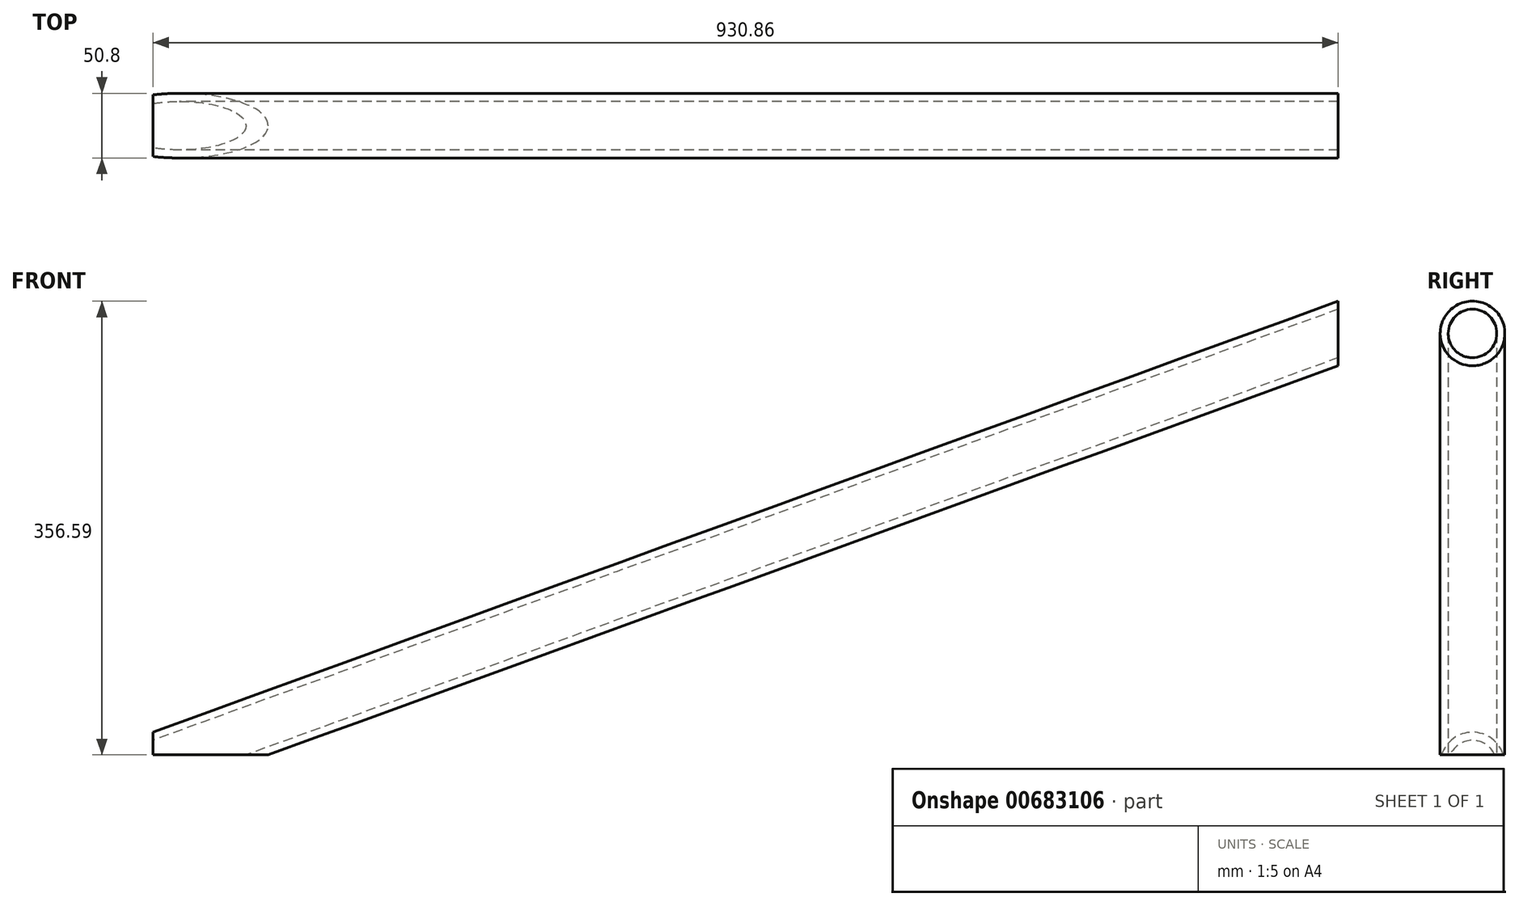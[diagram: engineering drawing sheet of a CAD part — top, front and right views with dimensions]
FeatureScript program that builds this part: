
annotation { "Feature Type Name" : "Feature", "Feature Type Description" : "" }
export const myFeature = defineFeature(function(context is Context, id is Id, definition is map)
    precondition{}
    {
        {
            var Q0;
            Q0=qCreatedBy(makeId("Front.planeOp"),FACE);
            var sketch = newSketch(context, id + "F0", { "sketchPlane" : qUnion([Q0])});
            skLineSegment(sketch, "E0", {"start": v(0, 0) * mm, "end": v(930.86, 338.8) * mm});
            skSolve(sketch);
        }
        {
            var Q0;
            Q0=qCreatedBy(makeId("Right.planeOp"),FACE);
            var sketch = newSketch(context, id + "F1", { "sketchPlane" : qUnion([Q0])});
            skCircle(sketch, "E1", {"center": v(0, 0) * mm, "radius": 25.4 * mm});
            skCircle(sketch, "E2", {"center": v(0, 0) * mm, "radius": 19.05 * mm});
            skSolve(sketch);
        }
        {
            var Q0;
            Q0=makeQuery(id+"F1.imprint","IMPRINT",FACE,{"disambiguationData":[TD([[makeQuery(id+"F1.imprint","IMPRINT",EDGE,{"derivedFrom":sQuery(id+"F1.wireOp",EDGE,"E1")}),1.0]])]});
            var Q1;
            Q1=sQuery(id+"F0.wireOp",EDGE,"E0");
            sweep(context, id + "F2", {"profiles" : qUnion([Q0]), "path" : qUnion([Q1])});
        }
        {
            var Q0;
            Q0=makeQuery(id+"F2.opSweep","CAP_FACE",FACE,{"disambiguationData":[OSD([sQuery(id+"F0.wireOp",VERTEX,"E0.start"),sQuery(id+"F1.wireOp",EDGE,"E1"),sQuery(id+"F1.wireOp",EDGE,"E2")])],"isStart":true});
            var sketch = newSketch(context, id + "F3", { "sketchPlane" : qUnion([Q0])});
            skLineSegment(sketch, "E3.bottom", {"start": v(-25.4, 7.62) * mm, "end": v(25.4, 7.62) * mm});
            skLineSegment(sketch, "E3.top", {"start": v(-25.4, -25.4) * mm, "end": v(25.4, -25.4) * mm});
            skLineSegment(sketch, "E3.left", {"start": v(-25.4, 7.62) * mm, "end": v(-25.4, -25.4) * mm});
            skLineSegment(sketch, "E3.right", {"start": v(25.4, 7.62) * mm, "end": v(25.4, -25.4) * mm});
            skSolve(sketch);
        }
        {
            var Q0;
            Q0 = qSketchRegion(id + "F3", true);
            extrude(context, id + "F4", {"entities" : qUnion([Q0]), "operationType" : NewBodyOperationType.REMOVE, "endBound" : BoundingType.THROUGH_ALL, "oppositeDirection" : true, "depth" : 25.4 * mm, "offsetDistance" : 25.4 * mm});
        }
    });
